# Revit family: Franke_Kühleinheit_SU05_CM-A200_FM_CM
name_source: partatom
category: Sonderausstattung
revit_build: Autodesk Revit 2015 (Build: 20140606_1530(x64)
units: mm (PartAtom-declared; Revit-internal decimal feet)

## types (2) — shared parameters
Anzahl der Nullleiter = 1
Anzahl der Schutzleiter = 1
Anzahl von Polen = 1
Aufstellgewicht = 25 kg
Bauelement = Beistellgerät Kühleinheit SU05
Baugruppenkennzeichen = Beistellgerät Kühleinheit SU05
Beschreibung = Beistellgerät Kühleinheit SU05 dient zum Aufbewahren von vorgekühlter Milch
Breite = 270 mm  [stored 0.885827 ft]
Energieverlust nach DIN18873 = 0.460 kWh/24 h - 230 V
Hersteller = Franke
Höhe = 544 mm
Leistung max. = 2300 W
Leistung min. = 1900 W
Milchvorrat = 5 l
Modell = 410871 - Kühleinheit SU05 CM - A200 FM CM
Netzfrequenz = 50 Hz
Netzfrequenz alternativ = 60 Hz
Sicherung = 16 A
Spannung max. = 240 V
Spannung min. = 220 V
Temperaturberecih = + 3° C bis +8° C
Tiefe = 475 mm  [stored 1.5584 ft]
URL = http://www.franke.com
zero-valued in all types: Kosten

## per-type parameters (varying)
| type | Abdeckung |
| Kühleinheit SU05 CM - A200 FM CM(220-240V/black line/EU) | Franke Black |
| Kühleinheit SU05 CM - A200 FM CM(220-240V/anthrazit/EU) | Franke Anthrazit |

note: [stored X ft] marks values corroborated as IEEE doubles in the binary element streams (Revit-internal decimal feet)
